# Revit family: Seat_Cover_Dispenser-Bobrick-Fino_Collection-B-9221_Series
name_source: partatom
category: Specialty Equipment
units: mm (PartAtom-declared; Revit-internal decimal feet)

## family parameters
Cut with Voids When Loaded = No
Host = Face
OmniClass Number = 23.40.20.21
OmniClass Title = Toilet and Bath Specialties
Part Type = Normal
Room Calculation Point = No
Round Connector Dimension = Use Diameter
Shared = Yes

## types (2) — shared parameters
ADA = Yes
ADA Compliant = Yes
Assembly Code = C1030200
Capacity = 250 toilet seat covers or one box.
Default Elevation = 0"
Description = Surface-Mounted Seat-Cover Dispenser
Height = 11"
Installation Type = Surface Mounted
Length = 15 13/16"
Manufacturer = Bobrick
Mounting Height = 28 1/2"
Type Comments = Provide a 5'' (125mm) minimum clearance from bottom of dispenser to top of any horizontal projection to provide room for filling dispenser from bottom.
URL = http://www.bobrick.com
Warranty Information = 5-Year Limited Warranty — In addition to Bobrick’s one-year guarantee, Bobrick extends a limited 5-year warranty from the
date of purchase on all parts for model B-9221.
Width = 2"

## per-type parameters (varying)
| type | Finish | Material |
| B-9221 | Stainless Steel-Bobrick-Satin | Stainless Steel-Bobrick-Satin |
| B-9221.MBLK | Stainless Steel-Bobrick-Matte Black | Stainless Steel-Bobrick-Matte Black |

note: column(s) folded — value = type name in every type: Model

## geometry (parser evidence)
native form markers: Sweep x3
no freeform markers — native parametric forms only
